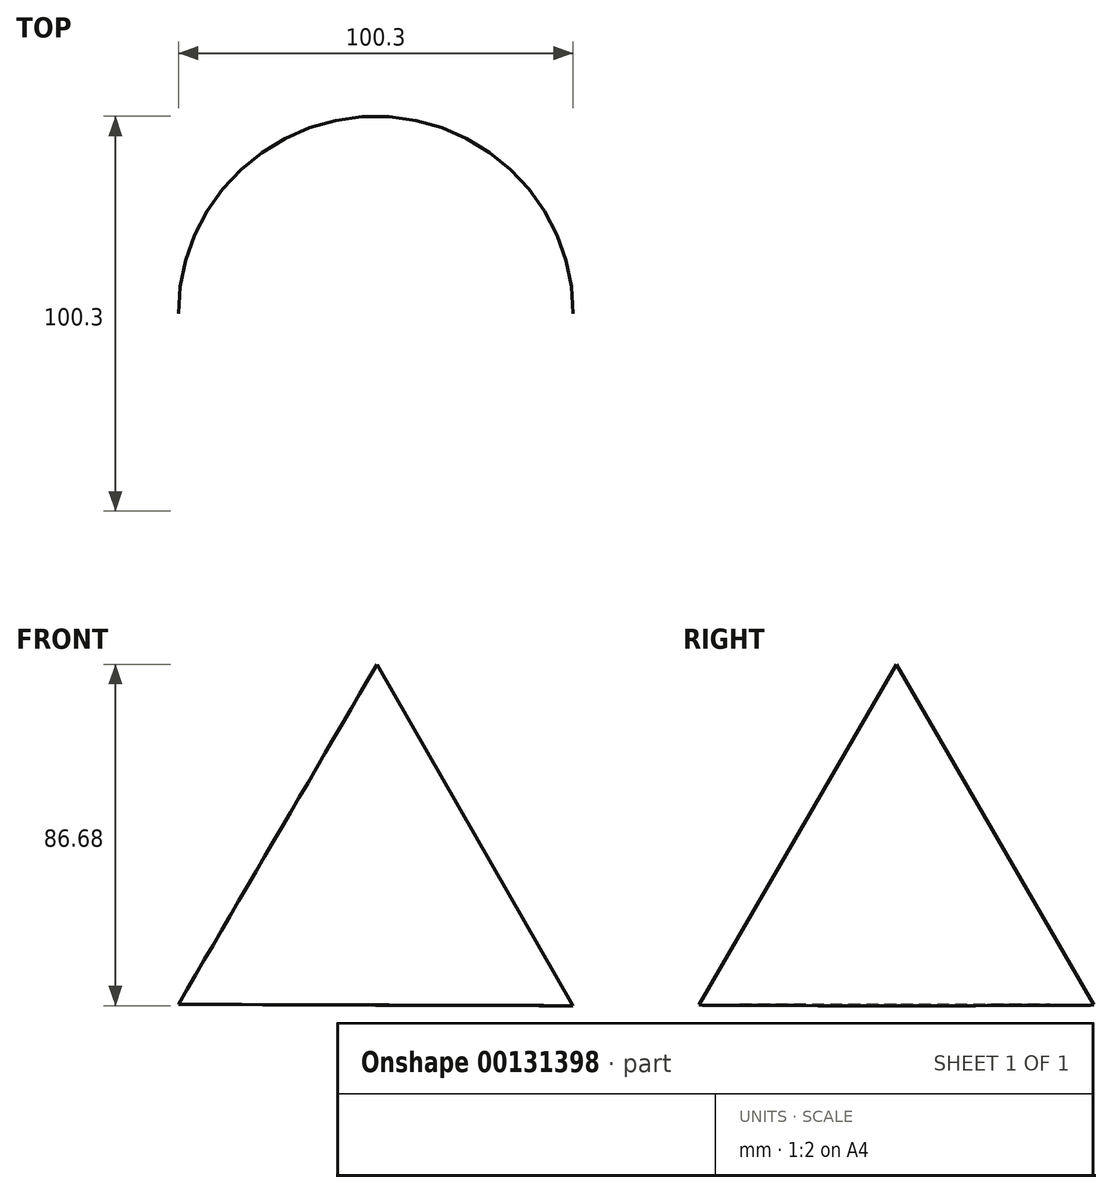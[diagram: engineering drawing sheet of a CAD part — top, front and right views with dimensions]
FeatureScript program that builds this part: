
annotation { "Feature Type Name" : "Feature", "Feature Type Description" : "" }
export const myFeature = defineFeature(function(context is Context, id is Id, definition is map)
    precondition{}
    {
        {
            var Q0;
            Q0=qCreatedBy(makeId("Front.planeOp"),FACE);
            var sketch = newSketch(context, id + "F0", { "sketchPlane" : qUnion([Q0])});
            skCircle(sketch, "E0.cCircle", {"center": v(0, 0) * mm, "radius": 28.87 * mm, "construction": true});
            skLineSegment(sketch, "E0.0", {"start": v(-50.15, -28.61) * mm, "end": v(0.3, 57.73) * mm});
            skLineSegment(sketch, "E0.1", {"start": v(0.3, 57.73) * mm, "end": v(49.85, -29.12) * mm});
            skLineSegment(sketch, "E0.2", {"start": v(49.85, -29.12) * mm, "end": v(-50.15, -28.61) * mm});
            skPoint(sketch, "E0.0.midPoint", {"position": v(-24.93, 14.56) * mm});
            skLineSegment(sketch, "E1", {"start": v(0.3, 57.73) * mm, "end": v(0, -28.87) * mm});
            skSolve(sketch);
        }
        {
            var Q0;
            {var subQ0=sQuery(id+"F0.wireOp",EDGE,"E0.0");Q0=makeQuery(id+"F0.imprint","IMPRINT",FACE,{"disambiguationData":[TD([[makeQuery(id+"F0.imprint","IMPRINT",EDGE,{"derivedFrom":subQ0}),-1.0]])]});}
            var Q1;
            Q1=sQuery(id+"F0.wireOp",EDGE,"E1");
            revolve(context, id + "F1", {"entities" : qUnion([Q0]), "axis" : qUnion([Q1]), "revolveType" : RevolveType.FULL});
        }
    });
